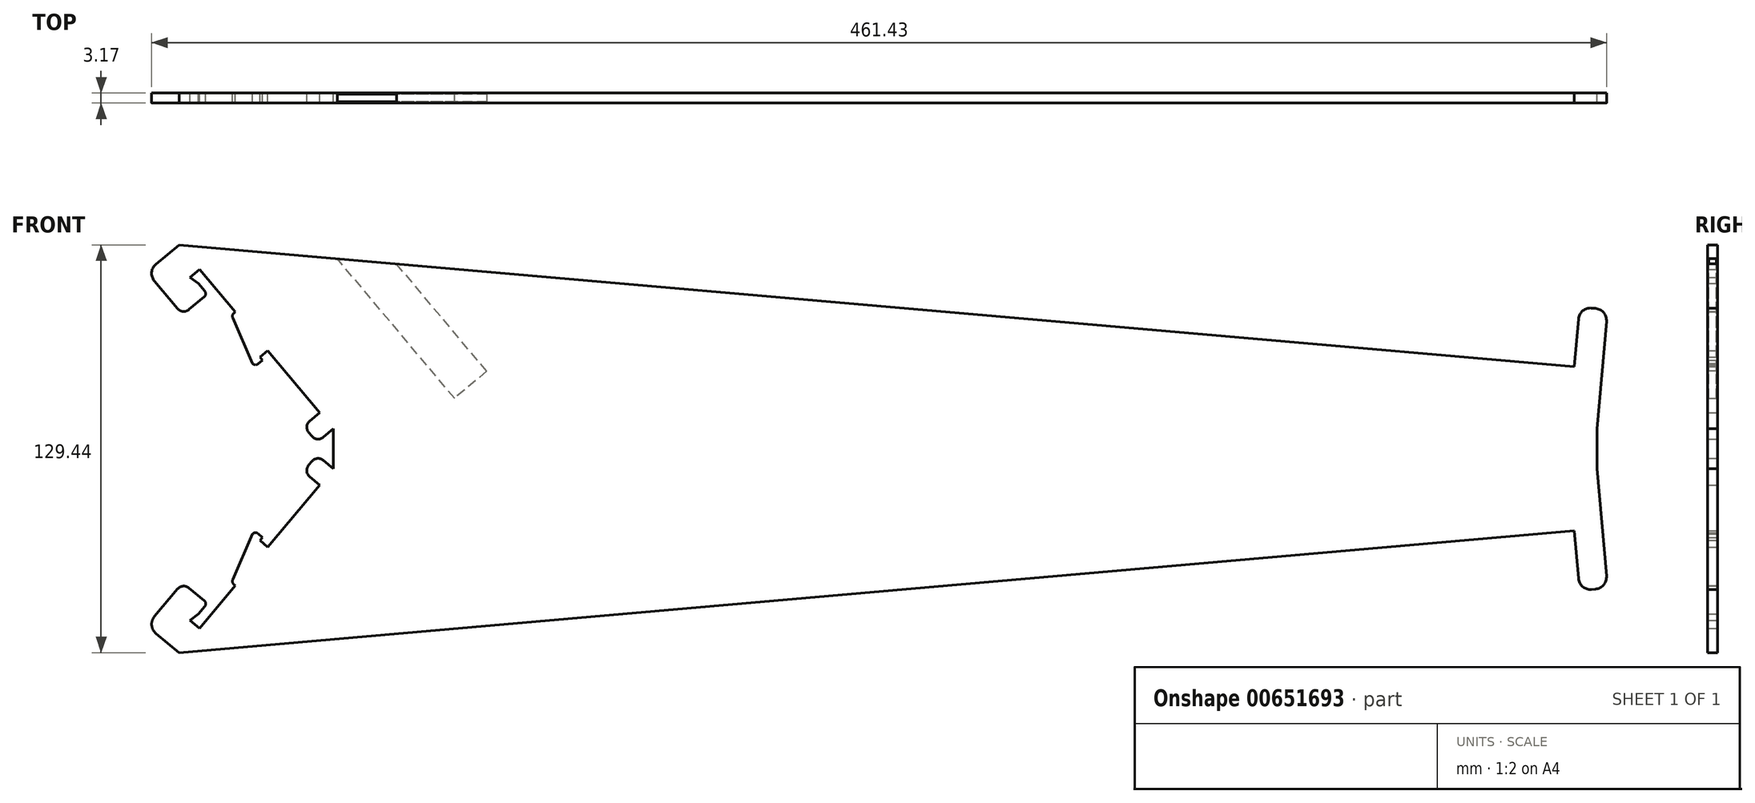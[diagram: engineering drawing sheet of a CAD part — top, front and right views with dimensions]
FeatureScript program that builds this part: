
annotation { "Feature Type Name" : "Feature", "Feature Type Description" : "" }
export const myFeature = defineFeature(function(context is Context, id is Id, definition is map)
    precondition{}
    {
        {
            var Q0;
            Q0=qCreatedBy(makeId("Front.planeOp"),FACE);
            var sketch = newSketch(context, id + "F0", { "sketchPlane" : qUnion([Q0])});
            skLineSegment(sketch, "E0.left", {"start": v(-46.53, -20.75) * mm, "end": v(-39.18, -29.5) * mm});
            skLineSegment(sketch, "E1", {"start": v(-38.77, -9.26) * mm, "end": v(403.81, -47.98) * mm});
            skLineSegment(sketch, "E2", {"start": v(403.81, -47.98) * mm, "end": v(405.14, -32.8) * mm});
            skLineSegment(sketch, "E3", {"start": v(10.22, -67.63) * mm, "end": v(411.02, -67.63) * mm});
            skPoint(sketch, "E4.start.orphan", {"position": v(-14.28, -38.44) * mm});
            skLineSegment(sketch, "E5.0", {"start": v(411.02, -67.63) * mm, "end": v(414, -33.57) * mm});
            skLineSegment(sketch, "E6.0", {"start": v(409.27, -29.33) * mm, "end": v(410.53, -29.44) * mm});
            skLineSegment(sketch, "E7", {"start": v(-46.06, -15.38) * mm, "end": v(-38.77, -9.26) * mm});
            skLineSegment(sketch, "E8", {"start": v(7, -70.32) * mm, "end": v(10.22, -67.63) * mm});
            skLineSegment(sketch, "E9.0", {"start": v(-12.22, -45.83) * mm, "end": v(-13.03, -44.86) * mm});
            skLineSegment(sketch, "E10.0", {"start": v(-35.6, -29.82) * mm, "end": v(-30.74, -25.73) * mm});
            skLineSegment(sketch, "E11.0", {"start": v(-30.58, -23.94) * mm, "end": v(-32.63, -21.51) * mm});
            skLineSegment(sketch, "E12.0", {"start": v(5.89, -62.47) * mm, "end": v(-10.6, -42.82) * mm});
            skLineSegment(sketch, "E13", {"start": v(-39.18, -29.5) * mm, "end": v(-46.53, -20.75) * mm});
            skLineSegment(sketch, "E14", {"start": v(-35.22, -19.55) * mm, "end": v(-32.23, -17.04) * mm});
            skPoint(sketch, "E15.newPointA", {"position": v(0, -76.2) * mm});
            skArc(sketch, "E15.filletArc", {"start": v(-39.18, -29.5) * mm, "mid": v(-37.46, -30.4) * mm, "end": v(-35.6, -29.82) * mm});
            skArc(sketch, "E16.filletArc", {"start": v(-30.74, -25.73) * mm, "mid": v(-30.3, -24.87) * mm, "end": v(-30.58, -23.94) * mm});
            skLineSegment(sketch, "E17.0", {"start": v(-13.03, -44.86) * mm, "end": v(-10.6, -42.82) * mm});
            skLineSegment(sketch, "E18.0", {"start": v(6.99, -43.82) * mm, "end": v(6.99, -43.82) * mm});
            skLineSegment(sketch, "E19.0", {"start": v(-13.68, -47.06) * mm, "end": v(-12.22, -45.83) * mm});
            skLineSegment(sketch, "E20.0", {"start": v(-21.37, -30.97) * mm, "end": v(-20.89, -30.56) * mm});
            skLineSegment(sketch, "E21", {"start": v(-21.72, -32.45) * mm, "end": v(-15.47, -46.9) * mm});
            skLineSegment(sketch, "E22.trimOffspring", {"start": v(-20.89, -30.56) * mm, "end": v(-32.23, -17.04) * mm});
            skLineSegment(sketch, "E23.0", {"start": v(2.68, -65.17) * mm, "end": v(5.89, -62.47) * mm});
            skLineSegment(sketch, "E24.0", {"start": v(3.43, -70) * mm, "end": v(2.37, -68.74) * mm});
            skPoint(sketch, "E25.visualSharp", {"position": v(0.73, -66.8) * mm});
            skArc(sketch, "E25.filletArc", {"start": v(2.68, -65.17) * mm, "mid": v(1.78, -66.9) * mm, "end": v(2.37, -68.74) * mm});
            skPoint(sketch, "E26.visualSharp", {"position": v(5.06, -71.96) * mm});
            skArc(sketch, "E26.filletArc", {"start": v(3.43, -70) * mm, "mid": v(5.15, -70.9) * mm, "end": v(7, -70.32) * mm});
            skPoint(sketch, "E27.visualSharp", {"position": v(-14.65, -47.87) * mm});
            skArc(sketch, "E27.filletArc", {"start": v(-15.47, -46.9) * mm, "mid": v(-14.6, -47.35) * mm, "end": v(-13.68, -47.06) * mm});
            skPoint(sketch, "E28.visualSharp", {"position": v(-22.1, -31.58) * mm});
            skArc(sketch, "E28.filletArc", {"start": v(-21.37, -30.97) * mm, "mid": v(-21.8, -31.65) * mm, "end": v(-21.72, -32.45) * mm});
            skPoint(sketch, "E29.visualSharp", {"position": v(414.33, -29.77) * mm});
            skArc(sketch, "E29.filletArc", {"start": v(414, -33.57) * mm, "mid": v(413.12, -30.79) * mm, "end": v(410.53, -29.44) * mm});
            skPoint(sketch, "E30.visualSharp", {"position": v(405.47, -29) * mm});
            skArc(sketch, "E30.filletArc", {"start": v(409.27, -29.33) * mm, "mid": v(406.49, -30.2) * mm, "end": v(405.14, -32.8) * mm});
            skPoint(sketch, "E31.visualSharp", {"position": v(-48.98, -17.83) * mm});
            skArc(sketch, "E31.filletArc", {"start": v(-46.06, -15.38) * mm, "mid": v(-47.4, -17.96) * mm, "end": v(-46.53, -20.75) * mm});
            skLineSegment(sketch, "E32", {"start": v(-32.63, -21.51) * mm, "end": v(-35.22, -19.55) * mm});
            skPoint(sketch, "E33.orphan", {"position": v(-34.67, -19.08) * mm});
            skLineSegment(sketch, "E34.MirrorCS", {"start": v(-12.22, -102.12) * mm, "end": v(-13.03, -103.1) * mm});
            skArc(sketch, "E35.MirrorCS", {"start": v(-30.74, -122.22) * mm, "mid": v(-30.3, -123.09) * mm, "end": v(-30.58, -124.01) * mm});
            skLineSegment(sketch, "E36.MirrorCS", {"start": v(-30.58, -124.01) * mm, "end": v(-32.63, -126.44) * mm});
            skLineSegment(sketch, "E37.MirrorCS", {"start": v(3.43, -77.95) * mm, "end": v(2.37, -79.21) * mm});
            skLineSegment(sketch, "E38.MirrorCS", {"start": v(-46.53, -127.21) * mm, "end": v(-39.18, -118.45) * mm});
            skArc(sketch, "E39.MirrorCS", {"start": v(2.68, -82.8) * mm, "mid": v(1.78, -81.07) * mm, "end": v(2.37, -79.21) * mm});
            skLineSegment(sketch, "E40.MirrorCS", {"start": v(-35.6, -118.14) * mm, "end": v(-30.74, -122.22) * mm});
            skLineSegment(sketch, "E41.MirrorCS", {"start": v(-32.63, -126.44) * mm, "end": v(-35.22, -128.41) * mm});
            skLineSegment(sketch, "E42.MirrorCS", {"start": v(-35.22, -128.41) * mm, "end": v(-32.23, -130.92) * mm});
            skLineSegment(sketch, "E43.MirrorCS", {"start": v(7, -77.63) * mm, "end": v(10.22, -80.33) * mm});
            skLineSegment(sketch, "E44.MirrorCS", {"start": v(-13.68, -100.9) * mm, "end": v(-12.22, -102.12) * mm});
            skLineSegment(sketch, "E45.MirrorCS", {"start": v(-21.37, -116.99) * mm, "end": v(-20.89, -117.4) * mm});
            skArc(sketch, "E46.MirrorCS", {"start": v(-15.47, -101.06) * mm, "mid": v(-14.6, -100.6) * mm, "end": v(-13.68, -100.9) * mm});
            skLineSegment(sketch, "E47.MirrorCS", {"start": v(-20.89, -117.4) * mm, "end": v(-32.23, -130.92) * mm});
            skArc(sketch, "E48.MirrorCS", {"start": v(3.43, -77.95) * mm, "mid": v(5.15, -77.05) * mm, "end": v(7, -77.63) * mm});
            skLineSegment(sketch, "E49.MirrorCS", {"start": v(-13.03, -103.1) * mm, "end": v(-10.6, -105.14) * mm});
            skArc(sketch, "E50.MirrorCS", {"start": v(-21.37, -116.99) * mm, "mid": v(-21.8, -116.3) * mm, "end": v(-21.72, -115.5) * mm});
            skLineSegment(sketch, "E51.MirrorCS", {"start": v(2.68, -82.8) * mm, "end": v(5.89, -85.48) * mm});
            skLineSegment(sketch, "E52.MirrorCS", {"start": v(-39.18, -118.45) * mm, "end": v(-46.53, -127.21) * mm});
            skArc(sketch, "E53.MirrorCS", {"start": v(-46.06, -132.58) * mm, "mid": v(-47.4, -130) * mm, "end": v(-46.53, -127.21) * mm});
            skLineSegment(sketch, "E54.MirrorCS", {"start": v(409.27, -118.63) * mm, "end": v(410.53, -118.52) * mm});
            skLineSegment(sketch, "E55.MirrorCS", {"start": v(-21.72, -115.5) * mm, "end": v(-15.47, -101.06) * mm});
            skArc(sketch, "E56.MirrorCS", {"start": v(409.27, -118.63) * mm, "mid": v(406.49, -117.75) * mm, "end": v(405.14, -115.16) * mm});
            skArc(sketch, "E57.MirrorCS", {"start": v(-39.18, -118.45) * mm, "mid": v(-37.46, -117.56) * mm, "end": v(-35.6, -118.14) * mm});
            skArc(sketch, "E58.MirrorCS", {"start": v(414, -114.39) * mm, "mid": v(413.12, -117.17) * mm, "end": v(410.53, -118.52) * mm});
            skLineSegment(sketch, "E59.MirrorCS", {"start": v(-46.06, -132.58) * mm, "end": v(-38.77, -138.7) * mm});
            skPoint(sketch, "E60.MirrorP", {"position": v(-34.67, -128.88) * mm});
            skLineSegment(sketch, "E61.MirrorCS", {"start": v(403.81, -99.98) * mm, "end": v(405.14, -115.16) * mm});
            skPoint(sketch, "E62.MirrorP", {"position": v(-14.65, -100.08) * mm});
            skPoint(sketch, "E63.MirrorP", {"position": v(0.73, -81.16) * mm});
            skPoint(sketch, "E64.MirrorP", {"position": v(-22.1, -116.38) * mm});
            skPoint(sketch, "E65.MirrorP", {"position": v(-48.98, -130.13) * mm});
            skLineSegment(sketch, "E66.MirrorCS", {"start": v(5.89, -85.48) * mm, "end": v(-10.6, -105.14) * mm});
            skPoint(sketch, "E67.MirrorP", {"position": v(-14.28, -109.51) * mm});
            skLineSegment(sketch, "E68.MirrorCS", {"start": v(411.02, -80.33) * mm, "end": v(414, -114.39) * mm});
            skPoint(sketch, "E69.MirrorP", {"position": v(0, -71.76) * mm});
            skPoint(sketch, "E70.MirrorP", {"position": v(5.06, -76) * mm});
            skLineSegment(sketch, "E71.MirrorCS", {"start": v(10.22, -80.33) * mm, "end": v(411.02, -80.33) * mm});
            skPoint(sketch, "E72.MirrorP", {"position": v(414.33, -118.18) * mm});
            skLineSegment(sketch, "E73.MirrorCS", {"start": v(-38.77, -138.7) * mm, "end": v(403.81, -99.98) * mm});
            skPoint(sketch, "E74.MirrorP", {"position": v(405.47, -118.96) * mm});
            skLineSegment(sketch, "E75", {"start": v(10.22, -67.63) * mm, "end": v(10.22, -80.33) * mm});
            skLineSegment(sketch, "E76", {"start": v(411.02, -67.63) * mm, "end": v(411.02, -80.33) * mm});
            skPoint(sketch, "E77.filletArc.end.orphan", {"position": v(411.32, -64.15) * mm});
            skPoint(sketch, "E77.filletArc.start.orphan", {"position": v(407.53, -67.63) * mm});
            skPoint(sketch, "E78.MirrorCS.end.orphan", {"position": v(411.32, -83.8) * mm});
            skPoint(sketch, "E78.MirrorCS.start.orphan", {"position": v(407.53, -80.33) * mm});
            skSolve(sketch);
        }
        {
            var Q0;
            Q0=qSketchRegion(id+"F0",true);
            extrude(context, id + "F1", {"entities" : qUnion([Q0]), "depth" : 3.17 * mm, "offsetDistance" : 25.4 * mm});
        }
        {
            var Q0;
            Q0=makeQuery(id+"F1.opExtrude","SWEPT_FACE",FACE,{"disambiguationData":[OSD([sQuery(id+"F0.wireOp",EDGE,"E7")])]});
            var sketch = newSketch(context, id + "F2", { "sketchPlane" : qUnion([Q0])});
            skLineSegment(sketch, "E79.0", {"start": v(0, -2.8) * mm, "end": v(13.34, -2.8) * mm});
            skLineSegment(sketch, "E80.0", {"start": v(13.34, -0.38) * mm, "end": v(0, -0.38) * mm});
            skLineSegment(sketch, "E81", {"start": v(13.34, -0.38) * mm, "end": v(13.34, -2.8) * mm});
            skLineSegment(sketch, "E82", {"start": v(0, -2.8) * mm, "end": v(0, -0.38) * mm});
            skSolve(sketch);
        }
        {
            var Q0;
            Q0=qSketchRegion(id+"F2",true);
            extrude(context, id + "F3", {"entities" : qUnion([Q0]), "operationType" : NewBodyOperationType.REMOVE, "oppositeDirection" : true, "depth" : 93.47 * mm, "offsetDistance" : 25.4 * mm});
        }
    });
